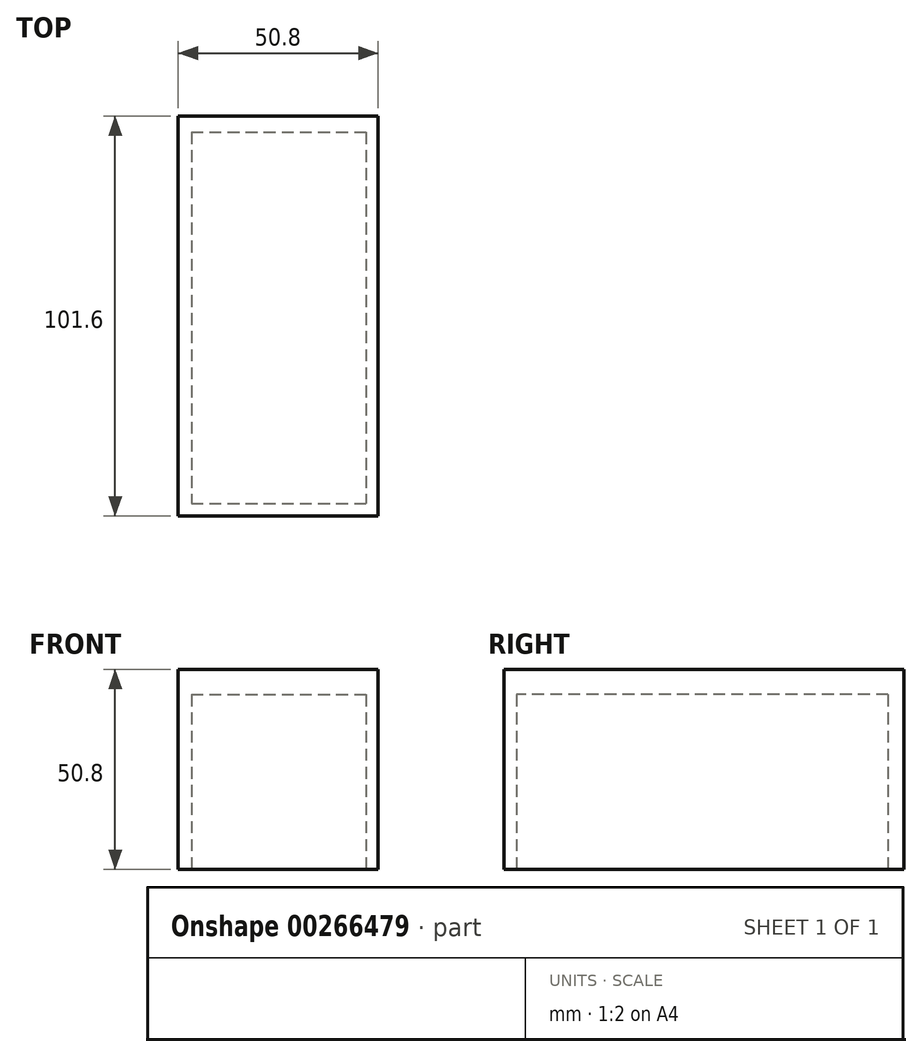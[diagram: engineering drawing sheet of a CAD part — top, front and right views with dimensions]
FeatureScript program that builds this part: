
annotation { "Feature Type Name" : "Feature", "Feature Type Description" : "" }
export const myFeature = defineFeature(function(context is Context, id is Id, definition is map)
    precondition{}
    {
        {
            var Q0;
            Q0=qCreatedBy(makeId("Front.planeOp"),FACE);
            var sketch = newSketch(context, id + "F0", { "sketchPlane" : qUnion([Q0])});
            skLineSegment(sketch, "E0.bottom", {"start": v(0, 0) * mm, "end": v(50.8, 0) * mm});
            skLineSegment(sketch, "E0.top", {"start": v(0, 50.8) * mm, "end": v(50.8, 50.8) * mm});
            skLineSegment(sketch, "E0.left", {"start": v(0, 0) * mm, "end": v(0, 50.8) * mm});
            skLineSegment(sketch, "E0.right", {"start": v(50.8, 0) * mm, "end": v(50.8, 50.8) * mm});
            skSolve(sketch);
        }
        {
            var Q0;
            Q0 = qSketchRegion(id + "F0", true);
            extrude(context, id + "F1", {"entities" : qUnion([Q0]), "depth" : 101.6 * mm});
        }
        {
            var Q0;
            Q0=qCreatedBy(makeId("Top.planeOp"),FACE);
            var sketch = newSketch(context, id + "F2", { "sketchPlane" : qUnion([Q0])});
            skLineSegment(sketch, "E1.bottom", {"start": v(3.34, -4.07) * mm, "end": v(47.77, -4.07) * mm});
            skLineSegment(sketch, "E1.top", {"start": v(3.34, -98.45) * mm, "end": v(47.77, -98.45) * mm});
            skLineSegment(sketch, "E1.left", {"start": v(3.34, -4.07) * mm, "end": v(3.34, -98.45) * mm});
            skLineSegment(sketch, "E1.right", {"start": v(47.77, -4.07) * mm, "end": v(47.77, -98.45) * mm});
            skSolve(sketch);
        }
        {
            var Q0;
            Q0 = qSketchRegion(id + "F2", true);
            extrude(context, id + "F3", {"entities" : qUnion([Q0]), "operationType" : NewBodyOperationType.REMOVE, "depth" : 44.45 * mm});
        }
    });
